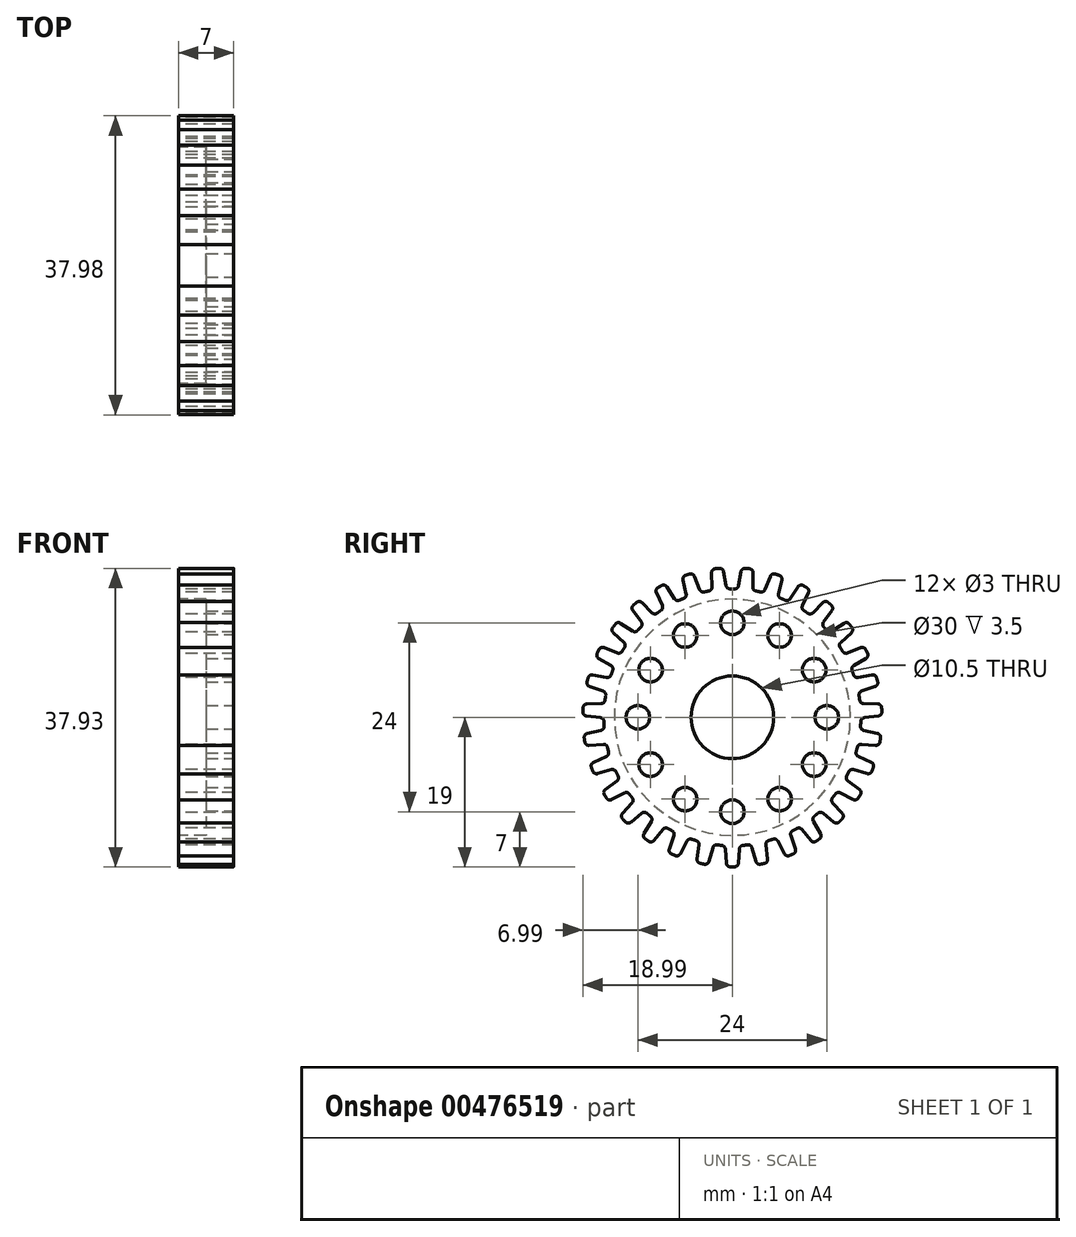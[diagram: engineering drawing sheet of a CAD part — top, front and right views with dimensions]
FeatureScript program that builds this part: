
annotation { "Feature Type Name" : "Feature", "Feature Type Description" : "" }
export const myFeature = defineFeature(function(context is Context, id is Id, definition is map)
    precondition{}
    {
        {
            var Q0;
            Q0=qCreatedBy(makeId("Front.planeOp"),FACE);
            var sketch = newSketch(context, id + "F0", { "sketchPlane" : qUnion([Q0])});
            skLineSegment(sketch, "E0.bottom", {"start": v(-3.5, 19) * mm, "end": v(3.5, 19) * mm});
            skLineSegment(sketch, "E0.top", {"start": v(0, 0) * mm, "end": v(3.5, 0) * mm});
            skLineSegment(sketch, "E0.left", {"start": v(-3.5, 19) * mm, "end": v(-3.5, 15) * mm});
            skLineSegment(sketch, "E0.right", {"start": v(3.5, 19) * mm, "end": v(3.5, 0) * mm});
            skPoint(sketch, "E1", {"position": v(0, 0) * mm});
            skLineSegment(sketch, "E2.top", {"start": v(-3.5, 15) * mm, "end": v(0, 15) * mm});
            skLineSegment(sketch, "E2.right", {"start": v(0, 0) * mm, "end": v(0, 15) * mm});
            skPoint(sketch, "E3.orphan", {"position": v(-3.5, 0) * mm});
            skSolve(sketch);
        }
        {
            var Q0;
            Q0=makeQuery(id+"F0.imprint","IMPRINT",FACE,{"disambiguationData":[TD([[makeQuery(id+"F0.imprint","IMPRINT",EDGE,{"derivedFrom":sQuery(id+"F0.wireOp",EDGE,"E0.bottom")}),-1.0]])]});
            var Q1;
            Q1=sQuery(id+"F0.wireOp",EDGE,"E0.top");
            revolve(context, id + "F1", {"entities" : qUnion([Q0]), "axis" : qUnion([Q1]), "revolveType" : RevolveType.FULL});
        }
        {
            var Q0;
            Q0=makeQuery(id+"F1.opRevolve","SWEPT_FACE",FACE,{"disambiguationData":[OSD([sQuery(id+"F0.wireOp",EDGE,"E0.right")])]});
            var sketch = newSketch(context, id + "F2", { "sketchPlane" : qUnion([Q0])});
            skCircle(sketch, "E4.0", {"center": v(0, 0) * mm, "radius": 19 * mm});
            skCircle(sketch, "E5", {"center": v(0, 0) * mm, "radius": 12 * mm, "construction": true});
            skPoint(sketch, "E6", {"position": v(0, 12) * mm});
            skPoint(sketch, "E7.1.0", {"position": v(-6, 10.4) * mm});
            skPoint(sketch, "E7.2.0", {"position": v(-10.4, 6) * mm});
            skPoint(sketch, "E7.3.0", {"position": v(-12, 0) * mm});
            skPoint(sketch, "E7.4.0", {"position": v(-10.4, -6) * mm});
            skPoint(sketch, "E7.5.0", {"position": v(-6, -10.4) * mm});
            skPoint(sketch, "E7.6.0", {"position": v(0, -12) * mm});
            skPoint(sketch, "E7.7.0", {"position": v(6, -10.4) * mm});
            skPoint(sketch, "E7.8.0", {"position": v(10.4, -6) * mm});
            skPoint(sketch, "E7.9.0", {"position": v(12, 0) * mm});
            skPoint(sketch, "E7.10.0", {"position": v(10.4, 6) * mm});
            skPoint(sketch, "E7.11.0", {"position": v(6, 10.4) * mm});
            skSolve(sketch);
        }
        {
            var Q0;
            Q0=sQuery(id+"F2.wireOp",VERTEX,"E6");
            var Q1;
            Q1=sQuery(id+"F2.wireOp",VERTEX,"E7.11.0");
            var Q2;
            Q2=sQuery(id+"F2.wireOp",VERTEX,"E7.10.0");
            var Q3;
            Q3=sQuery(id+"F2.wireOp",VERTEX,"E7.9.0");
            var Q4;
            Q4=sQuery(id+"F2.wireOp",VERTEX,"E7.8.0");
            var Q5;
            Q5=sQuery(id+"F2.wireOp",VERTEX,"E7.7.0");
            var Q6;
            Q6=sQuery(id+"F2.wireOp",VERTEX,"E7.6.0");
            var Q7;
            Q7=sQuery(id+"F2.wireOp",VERTEX,"E7.5.0");
            var Q8;
            Q8=sQuery(id+"F2.wireOp",VERTEX,"E7.4.0");
            var Q9;
            Q9=sQuery(id+"F2.wireOp",VERTEX,"E7.3.0");
            var Q10;
            Q10=sQuery(id+"F2.wireOp",VERTEX,"E7.2.0");
            var Q11;
            Q11=sQuery(id+"F2.wireOp",VERTEX,"E7.1.0");
            var Q12;
            Q12=makeQuery(id+"F1.opRevolve","SWEPT_BODY",BODY,{"disambiguationData":[OSD([sQuery(id+"F0.wireOp",EDGE,"E0.bottom"),sQuery(id+"F0.wireOp",EDGE,"E0.top"),sQuery(id+"F0.wireOp",EDGE,"E0.left"),sQuery(id+"F0.wireOp",EDGE,"E0.right"),sQuery(id+"F0.wireOp",EDGE,"E2.top"),sQuery(id+"F0.wireOp",EDGE,"E2.right")])]});
            hole(context, id + "F3", {"style" : HoleStyle.SIMPLE, "endStyle" : HoleEndStyle.THROUGH, "holeDiameter" : 3 * mm, "tappedDepth" : 13.9 * mm, "tapClearance" : 3, "startFromSketch" : true, "locations" : qUnion([Q0, Q1, Q2, Q3, Q4, Q5, Q6, Q7, Q8, Q9, Q10, Q11]), "scope" : qUnion([Q12])});
        }
        {
            var Q0;
            Q0=makeQuery(id+"F1.opRevolve","SWEPT_FACE",FACE,{"disambiguationData":[OSD([sQuery(id+"F0.wireOp",EDGE,"E0.left")])]});
            var sketch = newSketch(context, id + "F4", { "sketchPlane" : qUnion([Q0])});
            skPoint(sketch, "E8.0", {"position": v(0, 0) * mm});
            skArc(sketch, "E9", {"start": v(0.3, 16.32) * mm, "mid": v(0, 16.32) * mm, "end": v(-0.3, 16.32) * mm});
            skArc(sketch, "E10.0", {"start": v(-1.65, 18.93) * mm, "mid": v(0, -19) * mm, "end": v(1.65, 18.93) * mm});
            skLineSegment(sketch, "E11", {"start": v(0.8, 16.73) * mm, "end": v(1.12, 18.52) * mm});
            skLineSegment(sketch, "E12.MirrorCS", {"start": v(-0.8, 16.73) * mm, "end": v(-1.12, 18.52) * mm});
            skPoint(sketch, "E13.visualSharp", {"position": v(-1.2, 18.96) * mm});
            skArc(sketch, "E13.filletArc", {"start": v(-1.12, 18.52) * mm, "mid": v(-1.3, 18.83) * mm, "end": v(-1.65, 18.93) * mm});
            skPoint(sketch, "E14.visualSharp", {"position": v(-0.73, 16.3) * mm});
            skArc(sketch, "E14.filletArc", {"start": v(-0.8, 16.73) * mm, "mid": v(-0.63, 16.43) * mm, "end": v(-0.3, 16.32) * mm});
            skPoint(sketch, "E15.visualSharp", {"position": v(0.73, 16.3) * mm});
            skArc(sketch, "E15.filletArc", {"start": v(0.3, 16.32) * mm, "mid": v(0.63, 16.43) * mm, "end": v(0.8, 16.73) * mm});
            skPoint(sketch, "E16.visualSharp", {"position": v(1.2, 18.96) * mm});
            skArc(sketch, "E16.filletArc", {"start": v(1.65, 18.93) * mm, "mid": v(1.3, 18.83) * mm, "end": v(1.12, 18.52) * mm});
            skSolve(sketch);
        }
        {
            var Q0;
            Q0=makeQuery(id+"F4.imprint","IMPRINT",FACE,{"disambiguationData":[TD([[makeQuery(id+"F4.imprint","IMPRINT",EDGE,{"derivedFrom":sQuery(id+"F4.wireOp",EDGE,"E9")}),-1.0]])]});
            extrude(context, id + "F5", {"entities" : qUnion([Q0]), "oppositeDirection" : true, "depth" : 25 * mm});
        }
        {
            var Q0;
            Q0=qCreatedBy(makeId("Front.planeOp"),FACE);
            var sketch = newSketch(context, id + "F6", { "sketchPlane" : qUnion([Q0])});
            skLineSegment(sketch, "E17", {"start": v(0, 0) * mm, "end": v(21.89, 0) * mm});
            skSolve(sketch);
        }
        {
            var Q0;
            Q0=makeQuery(id+"F5.opExtrude","SWEPT_BODY",BODY,{"disambiguationData":[OSD([sQuery(id+"F0.wireOp",EDGE,"E0.bottom"),sQuery(id+"F0.wireOp",EDGE,"E0.left"),sQuery(id+"F4.wireOp",EDGE,"E9"),sQuery(id+"F4.wireOp",EDGE,"E11"),sQuery(id+"F4.wireOp",EDGE,"E12.MirrorCS"),sQuery(id+"F4.wireOp",EDGE,"E13.filletArc"),sQuery(id+"F4.wireOp",EDGE,"E14.filletArc"),sQuery(id+"F4.wireOp",EDGE,"E15.filletArc"),sQuery(id+"F4.wireOp",EDGE,"E16.filletArc")])]});
            var Q1;
            Q1=sQuery(id+"F6.wireOp",EDGE,"E17");
            circularPattern(context, id + "F7", {"operationType" : NewBodyOperationType.REMOVE, "entities" : qUnion([Q0]), "axis" : qUnion([Q1]), "angle" : 360 * degree, "instanceCount" : 31, "equalSpace" : true});
        }
        {
            var Q0;
            Q0=makeQuery(id+"F1.opRevolve","SWEPT_FACE",FACE,{"disambiguationData":[OSD([sQuery(id+"F0.wireOp",EDGE,"E0.right")])]});
            var sketch = newSketch(context, id + "F8", { "sketchPlane" : qUnion([Q0])});
            skPoint(sketch, "E18.0", {"position": v(0, 0) * mm});
            skSolve(sketch);
        }
        {
            var Q0;
            Q0=sQuery(id+"F8.wireOp",VERTEX,"E18.0");
            var Q1;
            Q1=makeQuery(id+"F1.opRevolve","SWEPT_BODY",BODY,{"disambiguationData":[OSD([sQuery(id+"F0.wireOp",EDGE,"E0.bottom"),sQuery(id+"F0.wireOp",EDGE,"E0.top"),sQuery(id+"F0.wireOp",EDGE,"E0.left"),sQuery(id+"F0.wireOp",EDGE,"E0.right"),sQuery(id+"F0.wireOp",EDGE,"E2.top"),sQuery(id+"F0.wireOp",EDGE,"E2.right")])]});
            hole(context, id + "F9", {"style" : HoleStyle.SIMPLE, "endStyle" : HoleEndStyle.THROUGH, "holeDiameter" : 10.5 * mm, "tappedDepth" : 13.9 * mm, "tapClearance" : 3, "startFromSketch" : true, "locations" : qUnion([Q0]), "scope" : qUnion([Q1])});
        }
    });
